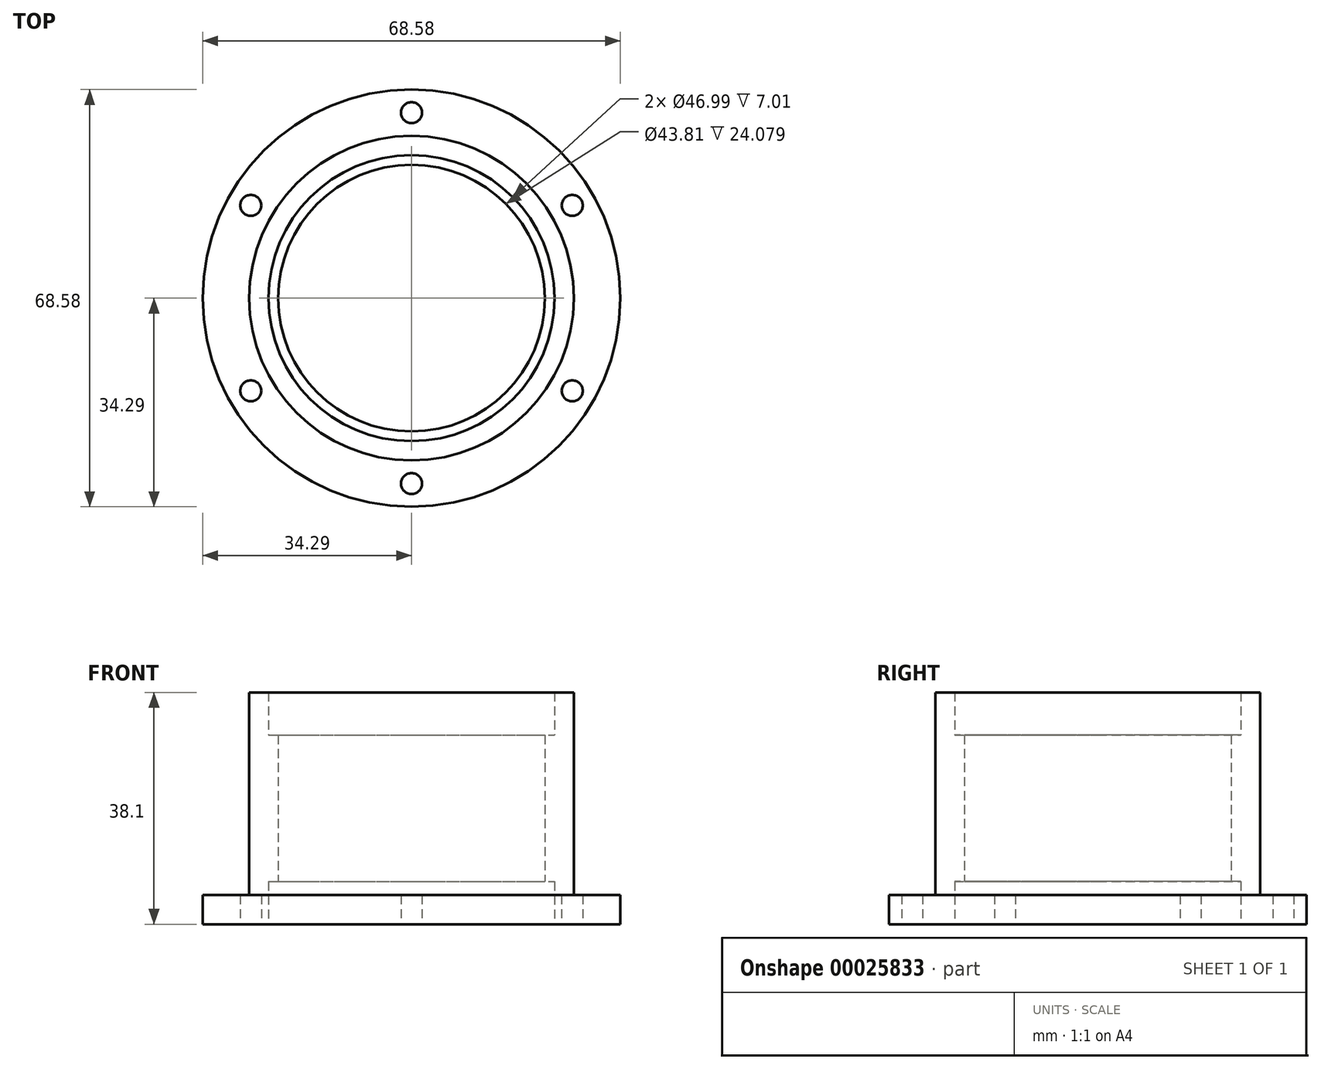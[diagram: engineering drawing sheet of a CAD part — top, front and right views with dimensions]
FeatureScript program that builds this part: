
annotation { "Feature Type Name" : "Feature", "Feature Type Description" : "" }
export const myFeature = defineFeature(function(context is Context, id is Id, definition is map)
    precondition{}
    {
        {
            var Q0;
            Q0=qCreatedBy(makeId("Front.planeOp"),FACE);
            var sketch = newSketch(context, id + "F0", { "sketchPlane" : qUnion([Q0])});
            skLineSegment(sketch, "E0", {"start": v(0, 0) * mm, "end": v(0, 48.1) * mm, "construction": true});
            skLineSegment(sketch, "E1", {"start": v(0, 0) * mm, "end": v(-34.3, 0) * mm, "construction": true});
            skLineSegment(sketch, "E2.bottom", {"start": v(-34.3, 0) * mm, "end": v(-23.5, 0) * mm});
            skLineSegment(sketch, "E2.top", {"start": v(-34.3, 4.78) * mm, "end": v(-26.67, 4.78) * mm});
            skLineSegment(sketch, "E2.left", {"start": v(-34.3, 0) * mm, "end": v(-34.3, 4.78) * mm});
            skLineSegment(sketch, "E3.top", {"start": v(-23.5, 38.1) * mm, "end": v(-26.67, 38.1) * mm});
            skLineSegment(sketch, "E3.right", {"start": v(-26.67, 4.78) * mm, "end": v(-26.67, 38.1) * mm});
            skLineSegment(sketch, "E4.bottom", {"start": v(-23.5, 31.09) * mm, "end": v(-21.9, 31.09) * mm});
            skLineSegment(sketch, "E4.top", {"start": v(-23.5, 7.01) * mm, "end": v(-21.9, 7.01) * mm});
            skLineSegment(sketch, "E4.right", {"start": v(-21.9, 31.09) * mm, "end": v(-21.9, 7.01) * mm});
            skLineSegment(sketch, "E5.trimOffspring", {"start": v(-23.5, 31.09) * mm, "end": v(-23.5, 38.1) * mm});
            skLineSegment(sketch, "E6", {"start": v(-23.5, 7.01) * mm, "end": v(-23.5, 0) * mm});
            skSolve(sketch);
        }
        {
            var Q0;
            Q0=makeQuery(id+"F0.imprint","IMPRINT",FACE,{"disambiguationData":[TD([[makeQuery(id+"F0.imprint","IMPRINT",EDGE,{"derivedFrom":sQuery(id+"F0.wireOp",EDGE,"E2.bottom")}),1.0]])]});
            var Q1;
            Q1=sQuery(id+"F0.wireOp",EDGE,"E0");
            revolve(context, id + "F1", {"entities" : qUnion([Q0]), "axis" : qUnion([Q1]), "revolveType" : RevolveType.FULL});
        }
        {
            var Q0;
            Q0=makeQuery(id+"F1.opRevolve","SWEPT_FACE",FACE,{"disambiguationData":[OSD([sQuery(id+"F0.wireOp",EDGE,"E2.bottom")])]});
            var sketch = newSketch(context, id + "F2", { "sketchPlane" : qUnion([Q0])});
            skLineSegment(sketch, "E7", {"start": v(0, 0) * mm, "end": v(0, 30.48) * mm});
            skLineSegment(sketch, "E8.1.0", {"start": v(0, 0) * mm, "end": v(-26.4, 15.24) * mm});
            skLineSegment(sketch, "E8.2.0", {"start": v(0, 0) * mm, "end": v(-26.4, -15.24) * mm});
            skLineSegment(sketch, "E8.3.0", {"start": v(0, 0) * mm, "end": v(0, -30.48) * mm});
            skLineSegment(sketch, "E8.4.0", {"start": v(0, 0) * mm, "end": v(26.4, -15.24) * mm});
            skLineSegment(sketch, "E8.5.0", {"start": v(0, 0) * mm, "end": v(26.4, 15.24) * mm});
            skPoint(sketch, "E8.center", {"position": v(0, 0) * mm});
            skSolve(sketch);
        }
        {
            var Q0;
            Q0=sQuery(id+"F2.wireOp",VERTEX,"E7.end");
            var Q1;
            Q1=sQuery(id+"F2.wireOp",VERTEX,"E8.1.0.end");
            var Q2;
            Q2=sQuery(id+"F2.wireOp",VERTEX,"E8.2.0.end");
            var Q3;
            Q3=sQuery(id+"F2.wireOp",VERTEX,"E8.3.0.end");
            var Q4;
            Q4=sQuery(id+"F2.wireOp",VERTEX,"E8.4.0.end");
            var Q5;
            Q5=sQuery(id+"F2.wireOp",VERTEX,"E8.5.0.end");
            var Q6;
            Q6=makeQuery(id+"F1.opRevolve","SWEPT_BODY",BODY,{"disambiguationData":[OSD([sQuery(id+"F0.wireOp",EDGE,"E2.bottom"),sQuery(id+"F0.wireOp",EDGE,"E2.top"),sQuery(id+"F0.wireOp",EDGE,"E2.left"),sQuery(id+"F0.wireOp",EDGE,"E3.top"),sQuery(id+"F0.wireOp",EDGE,"E3.right"),sQuery(id+"F0.wireOp",EDGE,"E4.bottom"),sQuery(id+"F0.wireOp",EDGE,"E4.top"),sQuery(id+"F0.wireOp",EDGE,"E4.right"),sQuery(id+"F0.wireOp",EDGE,"E5.trimOffspring"),sQuery(id+"F0.wireOp",EDGE,"E6")])]});
            hole(context, id + "F3", {"style" : HoleStyle.SIMPLE, "holeDiameter" : 3.45 * mm, "endStyle" : HoleEndStyle.THROUGH, "locations" : qUnion([Q0, Q1, Q2, Q3, Q4, Q5]), "scope" : qUnion([Q6])});
        }
    });
